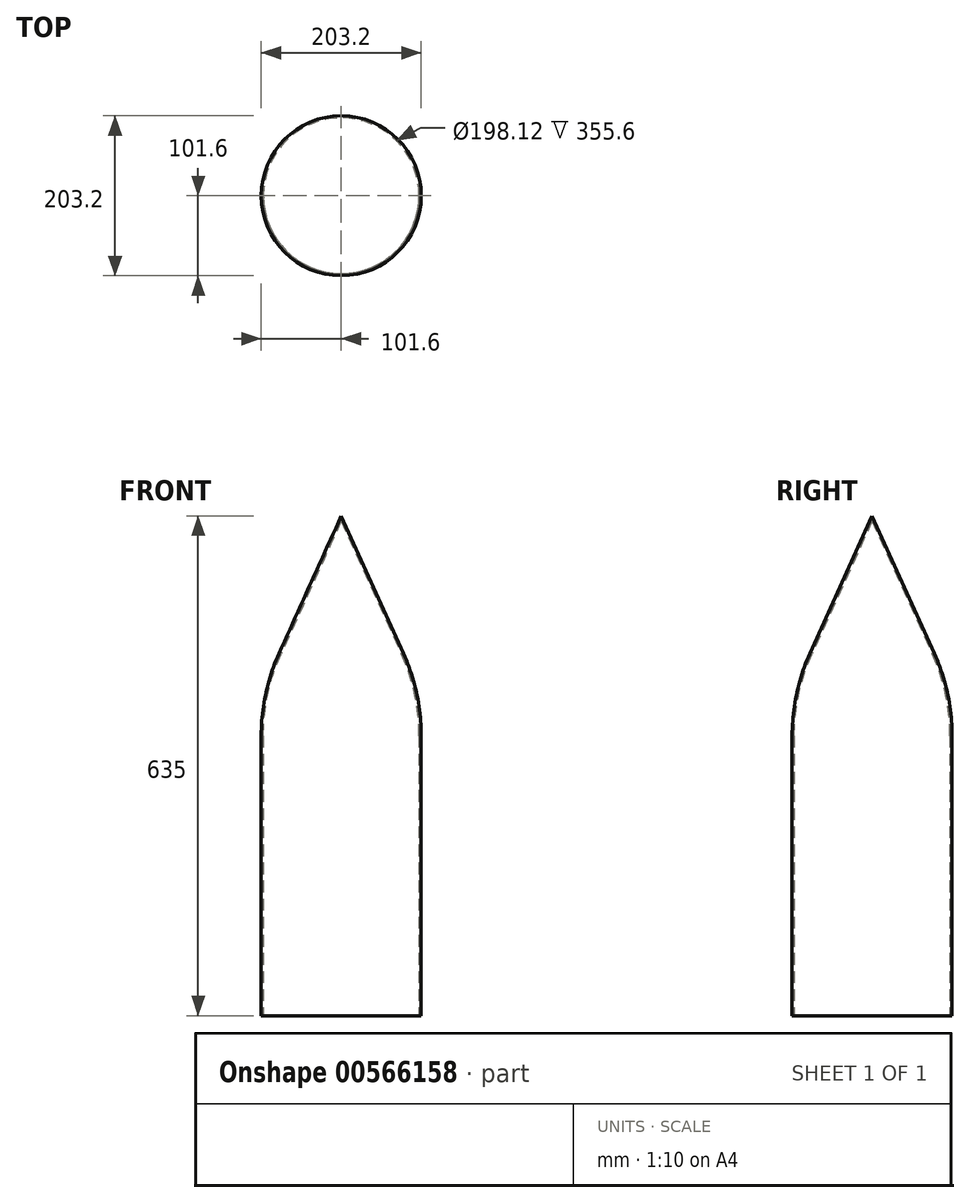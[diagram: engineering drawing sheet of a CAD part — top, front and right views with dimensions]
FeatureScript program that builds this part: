
annotation { "Feature Type Name" : "Feature", "Feature Type Description" : "" }
export const myFeature = defineFeature(function(context is Context, id is Id, definition is map)
    precondition{}
    {
        {
            var Q0;
            Q0=qCreatedBy(makeId("Right.planeOp"),FACE);
            var sketch = newSketch(context, id + "F0", { "sketchPlane" : qUnion([Q0])});
            skLineSegment(sketch, "E0", {"start": v(0, 0) * mm, "end": v(0, 635) * mm});
            skLineSegment(sketch, "E1", {"start": v(-101.6, 0) * mm, "end": v(-101.6, 355.6) * mm});
            skLineSegment(sketch, "E2", {"start": v(0, 635) * mm, "end": v(-79.03, 460.28) * mm});
            skPoint(sketch, "E3.visualSharp", {"position": v(-101.6, 410.37) * mm});
            skArc(sketch, "E3.filletArc", {"start": v(-79.03, 460.28) * mm, "mid": v(-95.9, 409.14) * mm, "end": v(-101.6, 355.6) * mm});
            skLineSegment(sketch, "E4", {"start": v(-101.6, 0) * mm, "end": v(0, 0) * mm});
            skSolve(sketch);
        }
        {
            var Q0;
            Q0 = qSketchRegion(id + "F0", true);
            var Q1;
            Q1=sQuery(id+"F0.wireOp",EDGE,"E0");
            revolve(context, id + "F1", {"entities" : qUnion([Q0]), "axis" : qUnion([Q1]), "revolveType" : RevolveType.FULL});
        }
        {
            var Q0;
            Q0=makeQuery(id+"F1.opRevolve","SWEPT_FACE",FACE,{"disambiguationData":[OSD([sQuery(id+"F0.wireOp",EDGE,"E4")])]});
            shell(context, id + "F2", {"entities" : qUnion([Q0]), "thickness" : 2.54 * mm});
        }
    });
